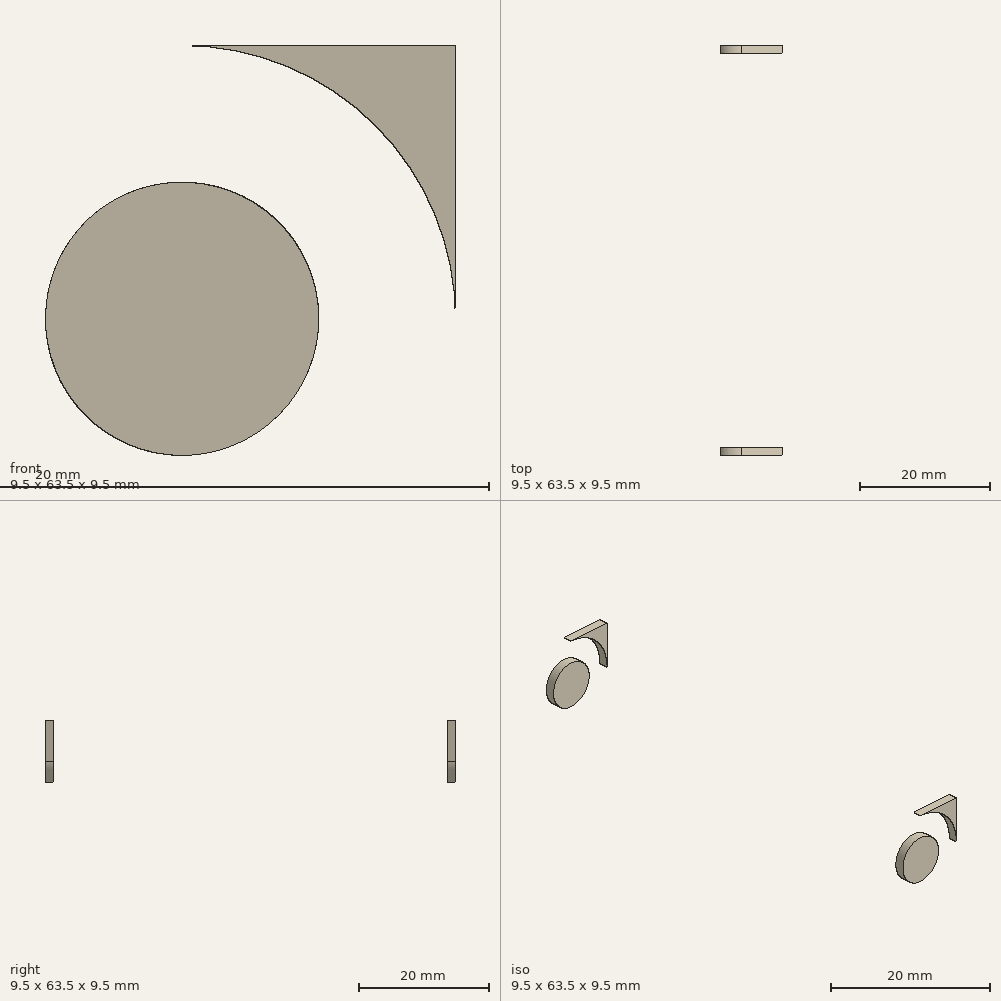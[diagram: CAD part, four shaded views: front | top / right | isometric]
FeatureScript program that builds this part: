
annotation { "Feature Type Name" : "Feature", "Feature Type Description" : "" }
export const myFeature = defineFeature(function(context is Context, id is Id, definition is map)
    precondition{}
    {
        {
            var Q0;
            Q0=qCreatedBy(makeId("Front.planeOp"),FACE);
            var sketch = newSketch(context, id + "F0", { "sketchPlane" : qUnion([Q0])});
            skLineSegment(sketch, "E0.bottom", {"start": v(0, 0) * mm, "end": v(-152.4, 0) * mm});
            skLineSegment(sketch, "E0.top", {"start": v(0, 12.7) * mm, "end": v(-152.4, 12.7) * mm});
            skLineSegment(sketch, "E0.left", {"start": v(0, 0) * mm, "end": v(0, 12.7) * mm});
            skLineSegment(sketch, "E0.right", {"start": v(-152.4, 0) * mm, "end": v(-152.4, 12.7) * mm});
            skSolve(sketch);
        }
        {
            var Q0;
            Q0=makeQuery(id+"F0.imprint","IMPRINT",FACE,{"disambiguationData":[TD([[makeQuery(id+"F0.imprint","IMPRINT",EDGE,{"derivedFrom":sQuery(id+"F0.wireOp",EDGE,"E0.bottom")}),-1.0]])]});
            extrude(context, id + "F1", {"entities" : qUnion([Q0]), "depth" : 63.5 * mm});
        }
        {
            var Q0;
            Q0=makeQuery(id+"F1.opExtrude","SWEPT_FACE",FACE,{"disambiguationData":[OSD([sQuery(id+"F0.wireOp",EDGE,"E0.top")])]});
            var sketch = newSketch(context, id + "F2", { "sketchPlane" : qUnion([Q0])});
            skLineSegment(sketch, "E1.0", {"start": v(0, 0) * mm, "end": v(-152.4, 0) * mm});
            skLineSegment(sketch, "E1.1", {"start": v(0, -63.5) * mm, "end": v(-152.4, -63.5) * mm});
            skLineSegment(sketch, "E1.2", {"start": v(-152.4, -63.5) * mm, "end": v(-152.4, 0) * mm});
            skLineSegment(sketch, "E1.3", {"start": v(0, -63.5) * mm, "end": v(0, 0) * mm});
            skLineSegment(sketch, "E2", {"start": v(0, -1.27) * mm, "end": v(-152.4, -1.27) * mm});
            skLineSegment(sketch, "E3", {"start": v(-152.4, -1.27) * mm, "end": v(-152.4, -62.23) * mm});
            skLineSegment(sketch, "E4", {"start": v(-152.4, -62.23) * mm, "end": v(0, -62.23) * mm});
            skSolve(sketch);
        }
        {
            var Q0;
            {var subQ0=sQuery(id+"F2.wireOp",EDGE,"E2");Q0=makeQuery(id+"F2.imprint","IMPRINT",FACE,{"disambiguationData":[TD([[makeQuery(id+"F2.imprint","IMPRINT",EDGE,{"derivedFrom":subQ0}),1.0]])]});}
            extrude(context, id + "F3", {"entities" : qUnion([Q0]), "operationType" : NewBodyOperationType.REMOVE, "oppositeDirection" : true, "depth" : 11.43 * mm});
        }
        {
            var Q0;
            Q0=makeQuery(id+"F1.opExtrude","CAP_FACE",FACE,{"disambiguationData":[OSD([sQuery(id+"F0.wireOp",EDGE,"E0.bottom"),sQuery(id+"F0.wireOp",EDGE,"E0.top"),sQuery(id+"F0.wireOp",EDGE,"E0.left"),sQuery(id+"F0.wireOp",EDGE,"E0.right")])],"isStart":false});
            var sketch = newSketch(context, id + "F4", { "sketchPlane" : qUnion([Q0])});
            skLineSegment(sketch, "E5.0", {"start": v(0, 12.7) * mm, "end": v(-152.4, 12.7) * mm});
            skLineSegment(sketch, "E5.1", {"start": v(-152.4, 0) * mm, "end": v(-152.4, 12.7) * mm});
            skLineSegment(sketch, "E5.2", {"start": v(0, 0) * mm, "end": v(-152.4, 0) * mm});
            skLineSegment(sketch, "E5.3", {"start": v(0, 0) * mm, "end": v(0, 12.7) * mm});
            skLineSegment(sketch, "E6", {"start": v(-76.2, 12.7) * mm, "end": v(-76.2, 0) * mm, "construction": true});
            skCircle(sketch, "E7", {"center": v(-146.05, 6.35) * mm, "radius": 3.18 * mm});
            skLineSegment(sketch, "E8", {"start": v(-146.05, 6.35) * mm, "end": v(-146.05, 12.7) * mm, "construction": true});
            skLineSegment(sketch, "E9", {"start": v(-146.05, 12.7) * mm, "end": v(-146.05, 6.35) * mm, "construction": true});
            skArc(sketch, "E10", {"start": v(-146.05, 12.7) * mm, "mid": v(-150.54, 10.84) * mm, "end": v(-152.4, 6.35) * mm});
            skCircle(sketch, "E11.MirrorC", {"center": v(-6.35, 6.35) * mm, "radius": 3.18 * mm});
            skArc(sketch, "E12.MirrorCS", {"start": v(-6.35, 12.7) * mm, "mid": v(-1.86, 10.84) * mm, "end": v(0, 6.35) * mm});
            skSolve(sketch);
        }
        {
            var Q0;
            Q0=makeQuery(id+"F3.boolean.opBoolean","COPY",EDGE,{"derivedFrom":makeQuery(id+"F3.opExtrude","CAP_EDGE",EDGE,{"disambiguationData":[OSD([sQuery(id+"F2.wireOp",EDGE,"E2")])],"isStart":false})});
            var Q1;
            Q1=makeQuery(id+"F3.boolean.opBoolean","COPY",EDGE,{"derivedFrom":makeQuery(id+"F3.opExtrude","CAP_EDGE",EDGE,{"disambiguationData":[OSD([sQuery(id+"F2.wireOp",EDGE,"E4")])],"isStart":false})});
            fillet(context, id + "F5", {"entities" : qUnion([Q0, Q1]), "radius" : 0.64 * mm, "tangentPropagation" : true, "allowEdgeOverflow" : false});
        }
        {
            var Q0;
            {var subQ3=sQuery(id+"F4.wireOp",EDGE,"E10");Q0=makeQuery(id+"F4.imprint","IMPRINT",FACE,{"disambiguationData":[TD([[makeQuery(id+"F4.imprint","IMPRINT",EDGE,{"derivedFrom":subQ3}),-1.0]])]});}
            var Q1;
            Q1=makeQuery(id+"F4.imprint","IMPRINT",FACE,{"disambiguationData":[TD([[makeQuery(id+"F4.imprint","IMPRINT",EDGE,{"derivedFrom":sQuery(id+"F4.wireOp",EDGE,"E7")}),1.0]])]});
            var Q2;
            {var subQ3=sQuery(id+"F4.wireOp",EDGE,"E12.MirrorCS");Q2=makeQuery(id+"F4.imprint","IMPRINT",FACE,{"disambiguationData":[TD([[makeQuery(id+"F4.imprint","IMPRINT",EDGE,{"derivedFrom":subQ3}),1.0]])]});}
            var Q3;
            Q3=makeQuery(id+"F4.imprint","IMPRINT",FACE,{"disambiguationData":[TD([[makeQuery(id+"F4.imprint","IMPRINT",EDGE,{"derivedFrom":sQuery(id+"F4.wireOp",EDGE,"E11.MirrorC")}),-1.0]])]});
            extrude(context, id + "F6", {"entities" : qUnion([Q0, Q1, Q2, Q3]), "operationType" : NewBodyOperationType.REMOVE, "endBound" : BoundingType.THROUGH_ALL, "oppositeDirection" : true, "depth" : 25.4 * mm});
        }
    });
